# Revit family: Doors_Industrial_BMP-Europe_PACK_200x350
name_source: partatom
category: Doors
revit_build: Autodesk Revit 2015 (Build: 20140606_1530(x64)
units: mm (PartAtom-declared; Revit-internal decimal feet)

## types (1)
- Doors_Industrial_BMP-Europe_PACK_200x350
    BIMobject category = Industrial
    BIMobject category code = doors-industrial
    BIMobject main category = Doors
    BIMobject main category code = doors
    Brand url = http://www.bmpdoors.com
    Control Panel (Left / Right) = Yes
    Date of publishing = 4/5/2019
    Design country = Italy
    Dimension A = 1098 mm  [stored 3.60236 ft]
    Edition number = 1
    Function = Interior
    Height = 5000 mm  [stored 16.4042 ft]
    IFC Classification = Door
    LOD100 = 5497 mm  [stored 18.0348 ft]
    Manufacturer country = Italy
    Manufacturer name = BMP Europe
    Masterformat 2014 Code = 08 11 16
    Masterformat 2014 Description = Aluminum Doors and Frames
    Material = <By Category>
    Material main = Aluminium
    Motor Left/Right = Yes
    Motor Placement (Front / Side) = Yes
    NBS Reference Code = 25-30-20-20
    NBS Reference Description = Doorset Systems
    Nominal height = 0 mm  [stored 0 ft]
    Nominal width = 0 mm  [stored 0 ft]
    OmniClass Code = 23-17 11 45 17
    OmniClass Description = Rapid Opening Doors
    Panel Height = 5930 mm  [stored 19.4554 ft]
    Product Guid = d73762e0-1a46-4f68-9f56-deec8d09e0de
    Product SKU = PACK
    Product data url = https://bimobject.com
    Product family = Doors / Industrial
    Product group = Fold-up doors - Megaimpack
    Product url = http://www.bmpeurope.eu
    QR code = http://bimobject.com
    Technical description = https://s3-eu-west-1.amazonaws.com
    UNSPSC Code = 30171503
    Uniclass 1.4 Code = JL20
    Uniclass 1.4 Description = Doors
    Uniclass 2.0 Code = SS-25-30-20-20
    Uniclass 2.0 Description = Doorset Systems
    Uniclass 2015 Code = Pr_30_59_24_04
    Uniclass 2015 Name = Automatic revolving doorsets
    Uniformat II Code = B2030
    Uniformat II Description = Exterior Doors
    Wall Closure = By host
    Weight Net (Kg) = 0
    Width = 5000 mm  [stored 16.4042 ft]
    Windows ON/OFF = Yes
    __Height = 5000 mm  [stored 16.4042 ft]
    __Opening Height = 0 mm  [stored 0 ft]
    __Width = 5000 mm  [stored 16.4042 ft]
    doubleMotor = No
    frontLeftMotor = Yes
    frontRightMotor = No
    lateralLeftMotor = No
    lateralRightMotor = No
    leftPanelVisibility = Yes
    minHeight = 8000 mm  [stored 26.2467 ft]
    minWidth = 5000 mm  [stored 16.4042 ft]
    motorLateral = No
    motorOffset = 5789 mm
    motorOffset2 = 5590 mm
    rightPanelVisibility = No
    transverseOffset = 3065 mm
    vis0 = No
    vis1 = No
    vis2 = Yes
    voidDistanceGate = 547 mm
    voidHelper = 798 mm  [stored 2.61811 ft]
    voidNumber = 4
    voidOpening = 1398 mm  [stored 4.58661 ft]
    voidOpening2 = 1398 mm  [stored 4.58661 ft]
    voidWidth = 850 mm  [stored 2.78871 ft]

note: [stored X ft] marks values corroborated as IEEE doubles in the binary element streams (Revit-internal decimal feet)

## geometry (parser evidence)
native form markers: Sweep x118
no freeform markers — native parametric forms only
